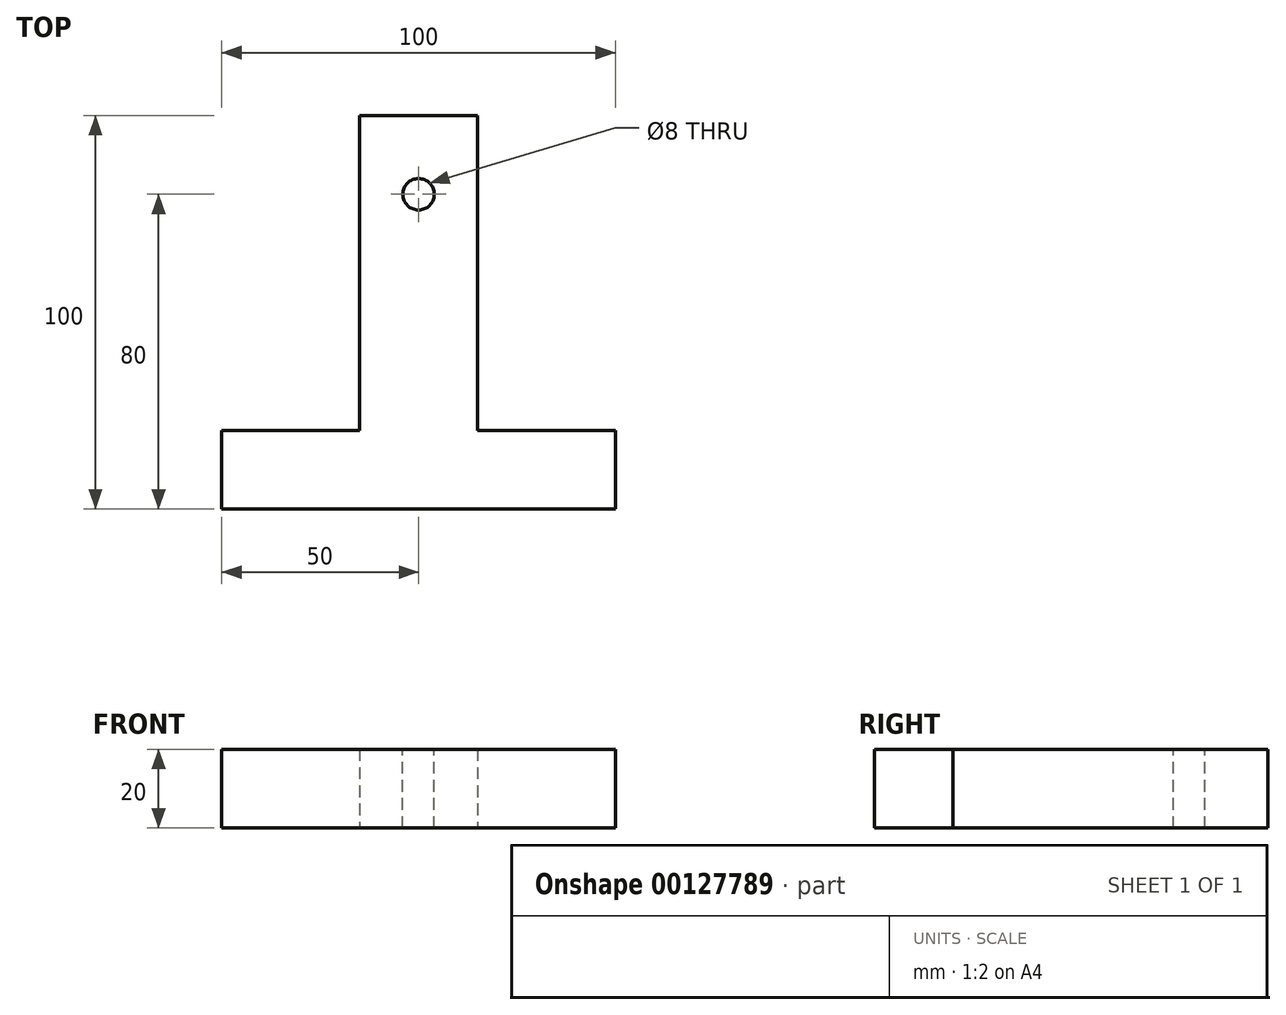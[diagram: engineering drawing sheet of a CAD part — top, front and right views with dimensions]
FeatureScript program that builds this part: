
annotation { "Feature Type Name" : "Feature", "Feature Type Description" : "" }
export const myFeature = defineFeature(function(context is Context, id is Id, definition is map)
    precondition{}
    {
        {
            var Q0;
            Q0=qCreatedBy(makeId("Top.planeOp"),FACE);
            var sketch = newSketch(context, id + "F0", { "sketchPlane" : qUnion([Q0])});
            skLineSegment(sketch, "E0", {"start": v(0, 0) * mm, "end": v(-50, 0) * mm});
            skLineSegment(sketch, "E1", {"start": v(-50, 0) * mm, "end": v(-50, 20) * mm});
            skLineSegment(sketch, "E2", {"start": v(-50, 20) * mm, "end": v(-15, 20) * mm});
            skLineSegment(sketch, "E3", {"start": v(-15, 20) * mm, "end": v(-15, 100) * mm});
            skLineSegment(sketch, "E4", {"start": v(-15, 100) * mm, "end": v(0, 100) * mm});
            skLineSegment(sketch, "E5", {"start": v(0, 0) * mm, "end": v(0, -30.4) * mm, "construction": true});
            skLineSegment(sketch, "E6.MirrorCS", {"start": v(0, 0) * mm, "end": v(50, 0) * mm});
            skLineSegment(sketch, "E7.MirrorCS", {"start": v(15, 100) * mm, "end": v(0, 100) * mm});
            skLineSegment(sketch, "E8.MirrorCS", {"start": v(50, 20) * mm, "end": v(15, 20) * mm});
            skLineSegment(sketch, "E9.MirrorCS", {"start": v(15, 20) * mm, "end": v(15, 100) * mm});
            skLineSegment(sketch, "E10.MirrorCS", {"start": v(50, 0) * mm, "end": v(50, 20) * mm});
            skSolve(sketch);
        }
        {
            var Q0;
            Q0 = qSketchRegion(id + "F0", true);
            extrude(context, id + "F1", {"entities" : qUnion([Q0]), "depth" : 20 * mm});
        }
        {
            var Q0;
            Q0=makeQuery(id+"F1.opExtrude","CAP_FACE",FACE,{"disambiguationData":[OSD([sQuery(id+"F0.wireOp",EDGE,"E0"),sQuery(id+"F0.wireOp",EDGE,"E1"),sQuery(id+"F0.wireOp",EDGE,"E2"),sQuery(id+"F0.wireOp",EDGE,"E3"),sQuery(id+"F0.wireOp",EDGE,"E4"),sQuery(id+"F0.wireOp",EDGE,"E6.MirrorCS"),sQuery(id+"F0.wireOp",EDGE,"E7.MirrorCS"),sQuery(id+"F0.wireOp",EDGE,"E8.MirrorCS"),sQuery(id+"F0.wireOp",EDGE,"E9.MirrorCS"),sQuery(id+"F0.wireOp",EDGE,"E10.MirrorCS")])],"isStart":false});
            var sketch = newSketch(context, id + "F2", { "sketchPlane" : qUnion([Q0])});
            skCircle(sketch, "E11", {"center": v(0, 80) * mm, "radius": 4 * mm});
            skSolve(sketch);
        }
        {
            var Q0;
            Q0 = qSketchRegion(id + "F2", true);
            extrude(context, id + "F3", {"entities" : qUnion([Q0]), "operationType" : NewBodyOperationType.REMOVE, "endBound" : BoundingType.THROUGH_ALL, "oppositeDirection" : true, "depth" : 25 * mm});
        }
    });
